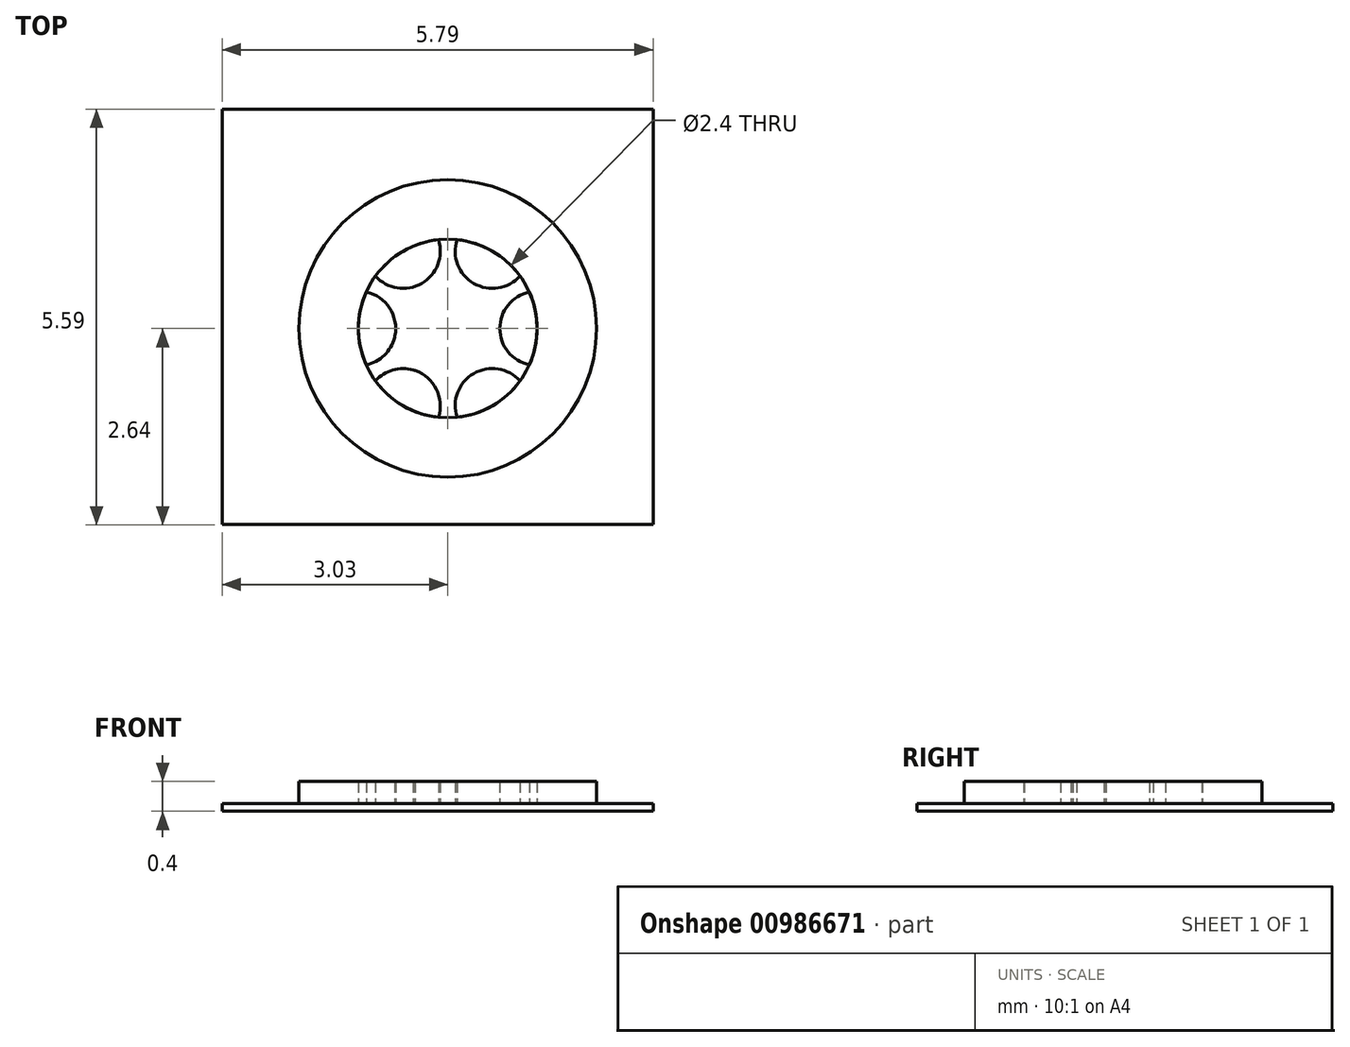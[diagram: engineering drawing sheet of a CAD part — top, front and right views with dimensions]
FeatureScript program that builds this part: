
annotation { "Feature Type Name" : "Feature", "Feature Type Description" : "" }
export const myFeature = defineFeature(function(context is Context, id is Id, definition is map)
    precondition{}
    {
        {
            var Q0;
            Q0=qCreatedBy(makeId("Top.planeOp"),FACE);
            var sketch = newSketch(context, id + "F0", { "sketchPlane" : qUnion([Q0])});
            skCircle(sketch, "E0", {"center": v(-1.2, 0) * mm, "radius": 0.5 * mm});
            skCircle(sketch, "E1.1.0", {"center": v(-0.6, -1.04) * mm, "radius": 0.5 * mm});
            skCircle(sketch, "E1.2.0", {"center": v(0.6, -1.04) * mm, "radius": 0.5 * mm});
            skCircle(sketch, "E1.3.0", {"center": v(1.2, 0) * mm, "radius": 0.5 * mm});
            skCircle(sketch, "E1.4.0", {"center": v(0.6, 1.04) * mm, "radius": 0.5 * mm});
            skCircle(sketch, "E1.5.0", {"center": v(-0.6, 1.04) * mm, "radius": 0.5 * mm});
            skPoint(sketch, "E1.center", {"position": v(0, 0) * mm});
            skCircle(sketch, "E2", {"center": v(0, 0) * mm, "radius": 1.2 * mm});
            skCircle(sketch, "E3", {"center": v(0, 0) * mm, "radius": 2 * mm});
            skCircle(sketch, "E4", {"center": v(-0.33, -0.2) * mm, "radius": 0.39 * mm});
            skPoint(sketch, "E4.second.point", {"position": v(-0.44, -0.57) * mm});
            skPoint(sketch, "E4.third.point", {"position": v(-0.7, -0.1) * mm});
            skLineSegment(sketch, "E5.bottom", {"start": v(-3.98, 2.65) * mm, "end": v(3.93, 2.65) * mm});
            skLineSegment(sketch, "E5.top", {"start": v(-3.98, -2.84) * mm, "end": v(3.93, -2.84) * mm});
            skLineSegment(sketch, "E5.left", {"start": v(-3.98, 2.65) * mm, "end": v(-3.98, -2.84) * mm});
            skLineSegment(sketch, "E5.right", {"start": v(3.93, 2.65) * mm, "end": v(3.93, -2.84) * mm});
            skSolve(sketch);
        }
        {
            var Q0;
            {var subQ0=sQuery(id+"F0.wireOp",EDGE,"E2");var subQ1=sQuery(id+"F0.wireOp",EDGE,"E1.5.0");var subQ2=makeQuery(id+"F0.imprint","INTERSECT",VERTEX,{"disambiguationData":[OD(0.0)],"derivedFrom":[subQ1,subQ0]});Q0=makeQuery(id+"F0.imprint","IMPRINT",FACE,{"disambiguationData":[TD([[makeQuery(id+"F0.imprint","IMPRINT",EDGE,{"disambiguationData":[TD([[subQ2,1.0]])],"derivedFrom":subQ1}),1.0]])]});}
            var Q1;
            {var subQ0=sQuery(id+"F0.wireOp",EDGE,"E2");var subQ1=sQuery(id+"F0.wireOp",EDGE,"E1.4.0");var subQ2=makeQuery(id+"F0.imprint","INTERSECT",VERTEX,{"disambiguationData":[OD(0.0)],"derivedFrom":[subQ1,subQ0]});Q1=makeQuery(id+"F0.imprint","IMPRINT",FACE,{"disambiguationData":[TD([[makeQuery(id+"F0.imprint","IMPRINT",EDGE,{"disambiguationData":[TD([[subQ2,1.0]])],"derivedFrom":subQ1}),1.0]])]});}
            var Q2;
            {var subQ0=sQuery(id+"F0.wireOp",EDGE,"E2");var subQ1=sQuery(id+"F0.wireOp",EDGE,"E1.3.0");var subQ2=makeQuery(id+"F0.imprint","INTERSECT",VERTEX,{"disambiguationData":[OD(0.0)],"derivedFrom":[subQ1,subQ0]});Q2=makeQuery(id+"F0.imprint","IMPRINT",FACE,{"disambiguationData":[TD([[makeQuery(id+"F0.imprint","IMPRINT",EDGE,{"disambiguationData":[TD([[subQ2,-1.0]])],"derivedFrom":subQ1}),1.0]])]});}
            var Q3;
            {var subQ0=sQuery(id+"F0.wireOp",EDGE,"E2");var subQ1=sQuery(id+"F0.wireOp",EDGE,"E1.2.0");var subQ2=makeQuery(id+"F0.imprint","INTERSECT",VERTEX,{"disambiguationData":[OD(0.0)],"derivedFrom":[subQ1,subQ0]});Q3=makeQuery(id+"F0.imprint","IMPRINT",FACE,{"disambiguationData":[TD([[makeQuery(id+"F0.imprint","IMPRINT",EDGE,{"disambiguationData":[TD([[subQ2,1.0]])],"derivedFrom":subQ1}),1.0]])]});}
            var Q4;
            {var subQ0=sQuery(id+"F0.wireOp",EDGE,"E2");var subQ1=sQuery(id+"F0.wireOp",EDGE,"E1.1.0");var subQ2=makeQuery(id+"F0.imprint","INTERSECT",VERTEX,{"disambiguationData":[OD(0.0)],"derivedFrom":[subQ1,subQ0]});Q4=makeQuery(id+"F0.imprint","IMPRINT",FACE,{"disambiguationData":[TD([[makeQuery(id+"F0.imprint","IMPRINT",EDGE,{"disambiguationData":[TD([[subQ2,1.0]])],"derivedFrom":subQ1}),1.0]])]});}
            var Q5;
            {var subQ0=sQuery(id+"F0.wireOp",EDGE,"E2");var subQ1=sQuery(id+"F0.wireOp",EDGE,"E0");var subQ2=makeQuery(id+"F0.imprint","INTERSECT",VERTEX,{"disambiguationData":[OD(0.0)],"derivedFrom":[subQ1,subQ0]});Q5=makeQuery(id+"F0.imprint","IMPRINT",FACE,{"disambiguationData":[TD([[makeQuery(id+"F0.imprint","IMPRINT",EDGE,{"disambiguationData":[TD([[subQ2,1.0]])],"derivedFrom":subQ1}),1.0]])]});}
            extrude(context, id + "F1", {"entities" : qUnion([Q0, Q1, Q2, Q3, Q4, Q5]), "depth" : 0.3 * mm, "offsetDistance" : 25 * mm});
        }
        {
            var Q0;
            Q0=makeQuery(id+"F0.imprint","IMPRINT",FACE,{"disambiguationData":[TD([[makeQuery(id+"F0.imprint","IMPRINT",EDGE,{"derivedFrom":sQuery(id+"F0.wireOp",EDGE,"E3")}),1.0]])]});
            var Q1;
            {var subQ0=sQuery(id+"F0.wireOp",EDGE,"E2");var subQ1=sQuery(id+"F0.wireOp",EDGE,"E0");var subQ2=makeQuery(id+"F0.imprint","INTERSECT",VERTEX,{"disambiguationData":[OD(0.0)],"derivedFrom":[subQ1,subQ0]});Q1=makeQuery(id+"F0.imprint","IMPRINT",FACE,{"disambiguationData":[TD([[makeQuery(id+"F0.imprint","IMPRINT",EDGE,{"disambiguationData":[TD([[subQ2,-1.0]])],"derivedFrom":subQ1}),1.0]])]});}
            var Q2;
            {var subQ0=sQuery(id+"F0.wireOp",EDGE,"E2");var subQ1=sQuery(id+"F0.wireOp",EDGE,"E1.1.0");var subQ2=makeQuery(id+"F0.imprint","INTERSECT",VERTEX,{"disambiguationData":[OD(0.0)],"derivedFrom":[subQ1,subQ0]});Q2=makeQuery(id+"F0.imprint","IMPRINT",FACE,{"disambiguationData":[TD([[makeQuery(id+"F0.imprint","IMPRINT",EDGE,{"disambiguationData":[TD([[subQ2,-1.0]])],"derivedFrom":subQ1}),1.0]])]});}
            var Q3;
            {var subQ0=sQuery(id+"F0.wireOp",EDGE,"E2");var subQ1=sQuery(id+"F0.wireOp",EDGE,"E1.2.0");var subQ2=makeQuery(id+"F0.imprint","INTERSECT",VERTEX,{"disambiguationData":[OD(0.0)],"derivedFrom":[subQ1,subQ0]});Q3=makeQuery(id+"F0.imprint","IMPRINT",FACE,{"disambiguationData":[TD([[makeQuery(id+"F0.imprint","IMPRINT",EDGE,{"disambiguationData":[TD([[subQ2,-1.0]])],"derivedFrom":subQ1}),1.0]])]});}
            var Q4;
            {var subQ0=sQuery(id+"F0.wireOp",EDGE,"E2");var subQ1=sQuery(id+"F0.wireOp",EDGE,"E1.3.0");var subQ2=makeQuery(id+"F0.imprint","INTERSECT",VERTEX,{"disambiguationData":[OD(0.0)],"derivedFrom":[subQ1,subQ0]});Q4=makeQuery(id+"F0.imprint","IMPRINT",FACE,{"disambiguationData":[TD([[makeQuery(id+"F0.imprint","IMPRINT",EDGE,{"disambiguationData":[TD([[subQ2,1.0]])],"derivedFrom":subQ1}),1.0]])]});}
            var Q5;
            {var subQ0=sQuery(id+"F0.wireOp",EDGE,"E2");var subQ1=sQuery(id+"F0.wireOp",EDGE,"E1.4.0");var subQ2=makeQuery(id+"F0.imprint","INTERSECT",VERTEX,{"disambiguationData":[OD(0.0)],"derivedFrom":[subQ1,subQ0]});Q5=makeQuery(id+"F0.imprint","IMPRINT",FACE,{"disambiguationData":[TD([[makeQuery(id+"F0.imprint","IMPRINT",EDGE,{"disambiguationData":[TD([[subQ2,-1.0]])],"derivedFrom":subQ1}),1.0]])]});}
            var Q6;
            {var subQ0=sQuery(id+"F0.wireOp",EDGE,"E2");var subQ1=sQuery(id+"F0.wireOp",EDGE,"E1.5.0");var subQ2=makeQuery(id+"F0.imprint","INTERSECT",VERTEX,{"disambiguationData":[OD(0.0)],"derivedFrom":[subQ1,subQ0]});Q6=makeQuery(id+"F0.imprint","IMPRINT",FACE,{"disambiguationData":[TD([[makeQuery(id+"F0.imprint","IMPRINT",EDGE,{"disambiguationData":[TD([[subQ2,-1.0]])],"derivedFrom":subQ1}),1.0]])]});}
            extrude(context, id + "F2", {"entities" : qUnion([Q0, Q1, Q2, Q3, Q4, Q5, Q6]), "depth" : 0.3 * mm, "offsetDistance" : 25 * mm});
        }
        {
            var Q0;
            {var subQ0=sQuery(id+"F0.wireOp",EDGE,"E4");var subQ1=sQuery(id+"F0.wireOp",EDGE,"E0");var subQ2=makeQuery(id+"F0.imprint","INTERSECT",VERTEX,{"disambiguationData":[OD(0.0)],"derivedFrom":[subQ1,subQ0]});Q0=makeQuery(id+"F0.imprint","IMPRINT",FACE,{"disambiguationData":[TD([[makeQuery(id+"F0.imprint","IMPRINT",EDGE,{"disambiguationData":[TD([[subQ2,1.0]])],"derivedFrom":subQ0}),1.0]])]});}
            var Q1;
            Q1=sQuery(id+"F0.wireOp",EDGE,"E4");
            extrude(context, id + "F3", {"entities" : qUnion([Q0]), "surfaceEntities" : qUnion([Q1]), "depth" : 0.3 * mm, "offsetDistance" : 25 * mm});
        }
        {
            var Q0;
            Q0=makeQuery(id+"F2.opExtrude","SWEPT_BODY",BODY,{"disambiguationData":[OSD([sQuery(id+"F0.wireOp",EDGE,"E0"),sQuery(id+"F0.wireOp",EDGE,"E2"),sQuery(id+"F0.wireOp",EDGE,"E3")])]});
            var Q1;
            Q1=makeQuery(id+"F1.opExtrude","SWEPT_BODY",BODY,{"disambiguationData":[OSD([sQuery(id+"F0.wireOp",EDGE,"E0"),sQuery(id+"F0.wireOp",EDGE,"E2")])]});
            booleanBodies(context, id + "F4", {"operationType" : BooleanOperationType.UNION, "tools" : qUnion([Q0, Q1])});
        }
        {
            var Q0;
            {var subQ0=sQuery(id+"F0.wireOp",EDGE,"E2");var subQ1=sQuery(id+"F0.wireOp",EDGE,"E0");Q0=makeQuery(id+"F4.opBoolean","MERGE",FACE,{"derivedFrom":[makeQuery(id+"F1.opExtrude","CAP_FACE",FACE,{"disambiguationData":[OSD([subQ1,subQ0])],"isStart":true}),makeQuery(id+"F2.opExtrude","CAP_FACE",FACE,{"disambiguationData":[OSD([subQ1,subQ0,sQuery(id+"F0.wireOp",EDGE,"E3")])],"isStart":true})]});}
            var sketch = newSketch(context, id + "F5", { "sketchPlane" : qUnion([Q0])});
            skLineSegment(sketch, "E6.bottom", {"start": v(-3.03, 2.64) * mm, "end": v(2.76, 2.64) * mm});
            skLineSegment(sketch, "E6.top", {"start": v(-3.03, -2.95) * mm, "end": v(2.76, -2.95) * mm});
            skLineSegment(sketch, "E6.left", {"start": v(-3.03, 2.64) * mm, "end": v(-3.03, -2.95) * mm});
            skLineSegment(sketch, "E6.right", {"start": v(2.76, 2.64) * mm, "end": v(2.76, -2.95) * mm});
            skSolve(sketch);
        }
        {
            var Q0;
            Q0 = qSketchRegion(id + "F5", true);
            extrude(context, id + "F6", {"entities" : qUnion([Q0]), "depth" : 0.1 * mm, "offsetDistance" : 25 * mm});
        }
    });
